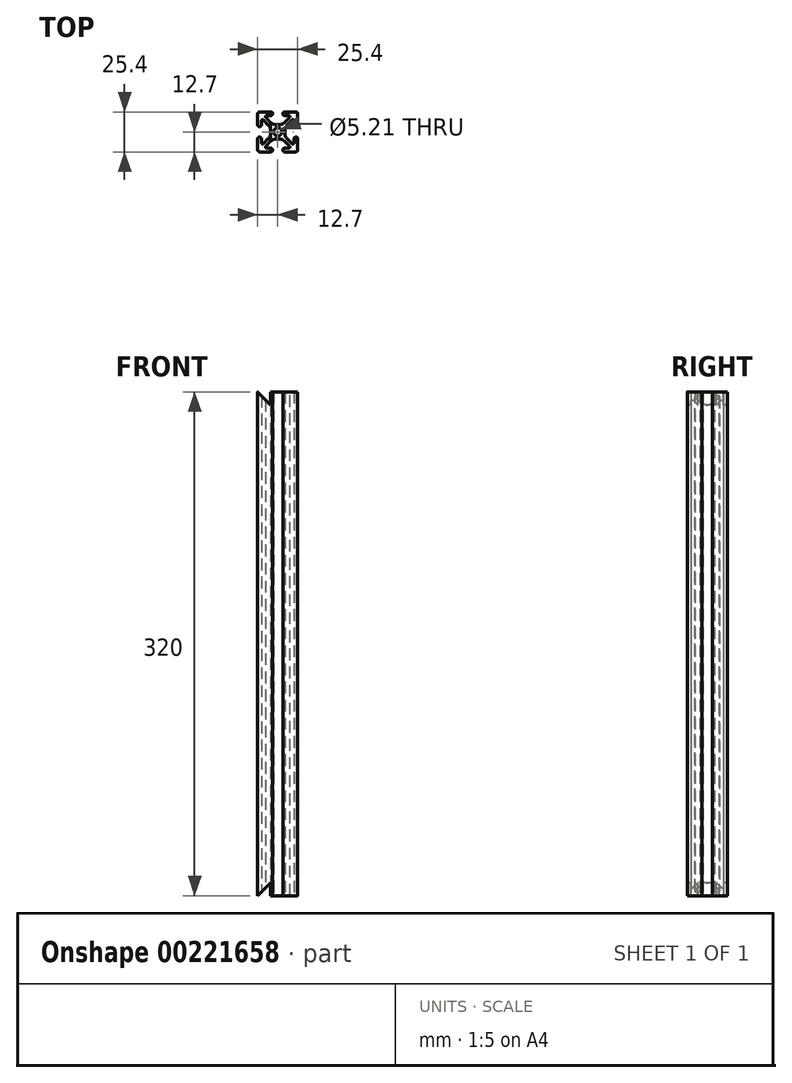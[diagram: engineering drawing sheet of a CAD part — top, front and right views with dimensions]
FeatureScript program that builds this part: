
annotation { "Feature Type Name" : "Feature", "Feature Type Description" : "" }
export const myFeature = defineFeature(function(context is Context, id is Id, definition is map)
    precondition{}
    {
        {
            var Q0;
            Q0=qCreatedBy(makeId("Top.planeOp"),FACE);
            var sketch = newSketch(context, id + "F0", { "sketchPlane" : qUnion([Q0])});
            skLineSegment(sketch, "E0.bottom", {"start": v(12.7, 12.7) * mm, "end": v(-12.7, 12.7) * mm});
            skLineSegment(sketch, "E0.top", {"start": v(12.7, -12.7) * mm, "end": v(-12.7, -12.7) * mm});
            skLineSegment(sketch, "E0.left", {"start": v(12.7, 12.7) * mm, "end": v(12.7, -12.7) * mm});
            skLineSegment(sketch, "E0.right", {"start": v(-12.7, 12.7) * mm, "end": v(-12.7, -12.7) * mm});
            skPoint(sketch, "E0.middle", {"position": v(0, 0) * mm});
            skCircle(sketch, "E1", {"center": v(0, 0) * mm, "radius": 2.6 * mm});
            skLineSegment(sketch, "E2", {"start": v(-12.7, 12.7) * mm, "end": v(12.7, -12.7) * mm, "construction": true});
            skLineSegment(sketch, "E3", {"start": v(0, 12.7) * mm, "end": v(0, -12.7) * mm, "construction": true});
            skLineSegment(sketch, "E4", {"start": v(-12.7, -12.7) * mm, "end": v(12.7, 12.7) * mm, "construction": true});
            skLineSegment(sketch, "E5", {"start": v(-8.78, 10.34) * mm, "end": v(-2.95, 4.5) * mm});
            skLineSegment(sketch, "E6.MirrorCS", {"start": v(8.78, 10.34) * mm, "end": v(2.95, 4.5) * mm});
            skLineSegment(sketch, "E7", {"start": v(-2.95, 4.5) * mm, "end": v(2.95, 4.5) * mm});
            skLineSegment(sketch, "E8.bottom", {"start": v(-3.24, 14.9) * mm, "end": v(3.24, 14.9) * mm});
            skLineSegment(sketch, "E8.left", {"start": v(-3.24, 14.9) * mm, "end": v(-3.24, 10.34) * mm});
            skLineSegment(sketch, "E8.right", {"start": v(3.24, 14.9) * mm, "end": v(3.24, 10.34) * mm});
            skLineSegment(sketch, "E9", {"start": v(-8.78, 10.34) * mm, "end": v(-3.24, 10.34) * mm});
            skLineSegment(sketch, "E10", {"start": v(3.24, 10.34) * mm, "end": v(8.78, 10.34) * mm});
            skLineSegment(sketch, "E11.MirrorCS", {"start": v(-10.34, 8.78) * mm, "end": v(-4.5, 2.95) * mm});
            skLineSegment(sketch, "E12.MirrorCS", {"start": v(-10.34, 8.78) * mm, "end": v(-10.34, 3.24) * mm});
            skLineSegment(sketch, "E13.MirrorCS", {"start": v(-14.9, 3.24) * mm, "end": v(-10.34, 3.24) * mm});
            skLineSegment(sketch, "E14.MirrorCS", {"start": v(-14.9, 3.24) * mm, "end": v(-14.9, -3.24) * mm});
            skLineSegment(sketch, "E15.MirrorCS", {"start": v(-14.9, -3.24) * mm, "end": v(-10.34, -3.24) * mm});
            skLineSegment(sketch, "E16.MirrorCS", {"start": v(-10.34, -3.24) * mm, "end": v(-10.34, -8.78) * mm});
            skLineSegment(sketch, "E17.MirrorCS", {"start": v(-10.34, -8.78) * mm, "end": v(-4.5, -2.95) * mm});
            skLineSegment(sketch, "E18.MirrorCS", {"start": v(-4.5, 2.95) * mm, "end": v(-4.5, -2.95) * mm});
            skLineSegment(sketch, "E19.MirrorCS", {"start": v(10.34, 8.78) * mm, "end": v(4.5, 2.95) * mm});
            skLineSegment(sketch, "E20.MirrorCS", {"start": v(4.5, -2.95) * mm, "end": v(4.5, 2.95) * mm});
            skLineSegment(sketch, "E21.MirrorCS", {"start": v(10.34, -8.78) * mm, "end": v(4.5, -2.95) * mm});
            skLineSegment(sketch, "E22.MirrorCS", {"start": v(10.34, -8.78) * mm, "end": v(10.34, -3.24) * mm});
            skLineSegment(sketch, "E23.MirrorCS", {"start": v(14.9, -3.24) * mm, "end": v(10.34, -3.24) * mm});
            skLineSegment(sketch, "E24.MirrorCS", {"start": v(14.9, -3.24) * mm, "end": v(14.9, 3.24) * mm});
            skLineSegment(sketch, "E25.MirrorCS", {"start": v(14.9, 3.24) * mm, "end": v(10.34, 3.24) * mm});
            skLineSegment(sketch, "E26.MirrorCS", {"start": v(10.34, 3.24) * mm, "end": v(10.34, 8.78) * mm});
            skLineSegment(sketch, "E27", {"start": v(-12.7, 0) * mm, "end": v(12.7, 0) * mm, "construction": true});
            skLineSegment(sketch, "E28.MirrorCS", {"start": v(-8.78, -10.34) * mm, "end": v(-2.95, -4.5) * mm});
            skLineSegment(sketch, "E29.MirrorCS", {"start": v(-8.78, -10.34) * mm, "end": v(-3.24, -10.34) * mm});
            skLineSegment(sketch, "E30.MirrorCS", {"start": v(-3.24, -14.9) * mm, "end": v(-3.24, -10.34) * mm});
            skLineSegment(sketch, "E31.MirrorCS", {"start": v(-3.24, -14.9) * mm, "end": v(3.24, -14.9) * mm});
            skLineSegment(sketch, "E32.MirrorCS", {"start": v(3.24, -14.9) * mm, "end": v(3.24, -10.34) * mm});
            skLineSegment(sketch, "E33.MirrorCS", {"start": v(3.24, -10.34) * mm, "end": v(8.78, -10.34) * mm});
            skLineSegment(sketch, "E34.MirrorCS", {"start": v(8.78, -10.34) * mm, "end": v(2.95, -4.5) * mm});
            skLineSegment(sketch, "E35.MirrorCS", {"start": v(-2.95, -4.5) * mm, "end": v(2.95, -4.5) * mm});
            skSolve(sketch);
        }
        {
            var Q0;
            Q0=makeQuery(id+"F0.imprint","IMPRINT",FACE,{"disambiguationData":[TD([[makeQuery(id+"F0.imprint","IMPRINT",EDGE,{"derivedFrom":sQuery(id+"F0.wireOp",EDGE,"E1")}),-1.0]])]});
            extrude(context, id + "F1", {"entities" : qUnion([Q0]), "depth" : 320 * mm});
        }
        {
            var Q0;
            Q0=makeQuery(id+"F1.opExtrude","SWEPT_EDGE",EDGE,{"disambiguationData":[OSD([sQuery(id+"F0.wireOp",EDGE,"E0.bottom"),sQuery(id+"F0.wireOp",EDGE,"E8.right")])]});
            var Q1;
            Q1=makeQuery(id+"F1.opExtrude","SWEPT_EDGE",EDGE,{"disambiguationData":[OSD([sQuery(id+"F0.wireOp",EDGE,"E8.right"),sQuery(id+"F0.wireOp",EDGE,"E10")])]});
            var Q2;
            Q2=makeQuery(id+"F1.opExtrude","SWEPT_EDGE",EDGE,{"disambiguationData":[OSD([sQuery(id+"F0.wireOp",EDGE,"E0.bottom"),sQuery(id+"F0.wireOp",EDGE,"E8.left")])]});
            var Q3;
            Q3=makeQuery(id+"F1.opExtrude","SWEPT_EDGE",EDGE,{"disambiguationData":[OSD([sQuery(id+"F0.wireOp",EDGE,"E0.right"),sQuery(id+"F0.wireOp",EDGE,"E13.MirrorCS")])]});
            var Q4;
            Q4=makeQuery(id+"F1.opExtrude","SWEPT_EDGE",EDGE,{"disambiguationData":[OSD([sQuery(id+"F0.wireOp",EDGE,"E8.left"),sQuery(id+"F0.wireOp",EDGE,"E9")])]});
            var Q5;
            Q5=makeQuery(id+"F1.opExtrude","SWEPT_EDGE",EDGE,{"disambiguationData":[OSD([sQuery(id+"F0.wireOp",EDGE,"E12.MirrorCS"),sQuery(id+"F0.wireOp",EDGE,"E13.MirrorCS")])]});
            var Q6;
            Q6=makeQuery(id+"F1.opExtrude","SWEPT_EDGE",EDGE,{"disambiguationData":[OSD([sQuery(id+"F0.wireOp",EDGE,"E0.left"),sQuery(id+"F0.wireOp",EDGE,"E25.MirrorCS")])]});
            var Q7;
            Q7=makeQuery(id+"F1.opExtrude","SWEPT_EDGE",EDGE,{"disambiguationData":[OSD([sQuery(id+"F0.wireOp",EDGE,"E25.MirrorCS"),sQuery(id+"F0.wireOp",EDGE,"E26.MirrorCS")])]});
            var Q8;
            Q8=makeQuery(id+"F1.opExtrude","SWEPT_EDGE",EDGE,{"disambiguationData":[OSD([sQuery(id+"F0.wireOp",EDGE,"E0.left"),sQuery(id+"F0.wireOp",EDGE,"E23.MirrorCS")])]});
            var Q9;
            Q9=makeQuery(id+"F1.opExtrude","SWEPT_EDGE",EDGE,{"disambiguationData":[OSD([sQuery(id+"F0.wireOp",EDGE,"E22.MirrorCS"),sQuery(id+"F0.wireOp",EDGE,"E23.MirrorCS")])]});
            var Q10;
            Q10=makeQuery(id+"F1.opExtrude","SWEPT_EDGE",EDGE,{"disambiguationData":[OSD([sQuery(id+"F0.wireOp",EDGE,"E32.MirrorCS"),sQuery(id+"F0.wireOp",EDGE,"E33.MirrorCS")])]});
            var Q11;
            Q11=makeQuery(id+"F1.opExtrude","SWEPT_EDGE",EDGE,{"disambiguationData":[OSD([sQuery(id+"F0.wireOp",EDGE,"E29.MirrorCS"),sQuery(id+"F0.wireOp",EDGE,"E30.MirrorCS")])]});
            var Q12;
            Q12=makeQuery(id+"F1.opExtrude","SWEPT_EDGE",EDGE,{"disambiguationData":[OSD([sQuery(id+"F0.wireOp",EDGE,"E15.MirrorCS"),sQuery(id+"F0.wireOp",EDGE,"E16.MirrorCS")])]});
            var Q13;
            Q13=makeQuery(id+"F1.opExtrude","SWEPT_EDGE",EDGE,{"disambiguationData":[OSD([sQuery(id+"F0.wireOp",EDGE,"E0.right"),sQuery(id+"F0.wireOp",EDGE,"E15.MirrorCS")])]});
            var Q14;
            Q14=makeQuery(id+"F1.opExtrude","SWEPT_EDGE",EDGE,{"disambiguationData":[OSD([sQuery(id+"F0.wireOp",EDGE,"E0.top"),sQuery(id+"F0.wireOp",EDGE,"E30.MirrorCS")])]});
            var Q15;
            Q15=makeQuery(id+"F1.opExtrude","SWEPT_EDGE",EDGE,{"disambiguationData":[OSD([sQuery(id+"F0.wireOp",EDGE,"E0.top"),sQuery(id+"F0.wireOp",EDGE,"E32.MirrorCS")])]});
            fillet(context, id + "F2", {"entities" : qUnion([Q0, Q1, Q2, Q3, Q4, Q5, Q6, Q7, Q8, Q9, Q10, Q11, Q12, Q13, Q14, Q15]), "radius" : 1.18 * mm, "tangentPropagation" : true, "allowEdgeOverflow" : false});
        }
        {
            var Q0;
            Q0=makeQuery(id+"F1.opExtrude","SWEPT_EDGE",EDGE,{"disambiguationData":[OSD([sQuery(id+"F0.wireOp",EDGE,"E6.MirrorCS"),sQuery(id+"F0.wireOp",EDGE,"E7")])]});
            var Q1;
            Q1=makeQuery(id+"F1.opExtrude","SWEPT_EDGE",EDGE,{"disambiguationData":[OSD([sQuery(id+"F0.wireOp",EDGE,"E5"),sQuery(id+"F0.wireOp",EDGE,"E7")])]});
            var Q2;
            Q2=makeQuery(id+"F1.opExtrude","SWEPT_EDGE",EDGE,{"disambiguationData":[OSD([sQuery(id+"F0.wireOp",EDGE,"E20.MirrorCS"),sQuery(id+"F0.wireOp",EDGE,"E21.MirrorCS")])]});
            var Q3;
            Q3=makeQuery(id+"F1.opExtrude","SWEPT_EDGE",EDGE,{"disambiguationData":[OSD([sQuery(id+"F0.wireOp",EDGE,"E19.MirrorCS"),sQuery(id+"F0.wireOp",EDGE,"E20.MirrorCS")])]});
            var Q4;
            Q4=makeQuery(id+"F1.opExtrude","SWEPT_EDGE",EDGE,{"disambiguationData":[OSD([sQuery(id+"F0.wireOp",EDGE,"E34.MirrorCS"),sQuery(id+"F0.wireOp",EDGE,"E35.MirrorCS")])]});
            var Q5;
            Q5=makeQuery(id+"F1.opExtrude","SWEPT_EDGE",EDGE,{"disambiguationData":[OSD([sQuery(id+"F0.wireOp",EDGE,"E28.MirrorCS"),sQuery(id+"F0.wireOp",EDGE,"E35.MirrorCS")])]});
            var Q6;
            Q6=makeQuery(id+"F1.opExtrude","SWEPT_EDGE",EDGE,{"disambiguationData":[OSD([sQuery(id+"F0.wireOp",EDGE,"E17.MirrorCS"),sQuery(id+"F0.wireOp",EDGE,"E18.MirrorCS")])]});
            var Q7;
            Q7=makeQuery(id+"F1.opExtrude","SWEPT_EDGE",EDGE,{"disambiguationData":[OSD([sQuery(id+"F0.wireOp",EDGE,"E11.MirrorCS"),sQuery(id+"F0.wireOp",EDGE,"E18.MirrorCS")])]});
            fillet(context, id + "F3", {"entities" : qUnion([Q0, Q1, Q2, Q3, Q4, Q5, Q6, Q7]), "radius" : 5.08 * mm, "tangentPropagation" : true, "allowEdgeOverflow" : false});
        }
        {
            var Q0;
            Q0=makeQuery(id+"F1.opExtrude","SWEPT_EDGE",EDGE,{"disambiguationData":[OSD([sQuery(id+"F0.wireOp",EDGE,"E6.MirrorCS"),sQuery(id+"F0.wireOp",EDGE,"E10")])]});
            var Q1;
            Q1=makeQuery(id+"F1.opExtrude","SWEPT_EDGE",EDGE,{"disambiguationData":[OSD([sQuery(id+"F0.wireOp",EDGE,"E5"),sQuery(id+"F0.wireOp",EDGE,"E9")])]});
            var Q2;
            Q2=makeQuery(id+"F1.opExtrude","SWEPT_EDGE",EDGE,{"disambiguationData":[OSD([sQuery(id+"F0.wireOp",EDGE,"E11.MirrorCS"),sQuery(id+"F0.wireOp",EDGE,"E12.MirrorCS")])]});
            var Q3;
            Q3=makeQuery(id+"F1.opExtrude","SWEPT_EDGE",EDGE,{"disambiguationData":[OSD([sQuery(id+"F0.wireOp",EDGE,"E16.MirrorCS"),sQuery(id+"F0.wireOp",EDGE,"E17.MirrorCS")])]});
            var Q4;
            Q4=makeQuery(id+"F1.opExtrude","SWEPT_EDGE",EDGE,{"disambiguationData":[OSD([sQuery(id+"F0.wireOp",EDGE,"E28.MirrorCS"),sQuery(id+"F0.wireOp",EDGE,"E29.MirrorCS")])]});
            var Q5;
            Q5=makeQuery(id+"F1.opExtrude","SWEPT_EDGE",EDGE,{"disambiguationData":[OSD([sQuery(id+"F0.wireOp",EDGE,"E33.MirrorCS"),sQuery(id+"F0.wireOp",EDGE,"E34.MirrorCS")])]});
            var Q6;
            Q6=makeQuery(id+"F1.opExtrude","SWEPT_EDGE",EDGE,{"disambiguationData":[OSD([sQuery(id+"F0.wireOp",EDGE,"E21.MirrorCS"),sQuery(id+"F0.wireOp",EDGE,"E22.MirrorCS")])]});
            var Q7;
            Q7=makeQuery(id+"F1.opExtrude","SWEPT_EDGE",EDGE,{"disambiguationData":[OSD([sQuery(id+"F0.wireOp",EDGE,"E19.MirrorCS"),sQuery(id+"F0.wireOp",EDGE,"E26.MirrorCS")])]});
            fillet(context, id + "F4", {"entities" : qUnion([Q0, Q1, Q2, Q3, Q4, Q5, Q6, Q7]), "radius" : 0.76 * mm, "tangentPropagation" : true, "allowEdgeOverflow" : false});
        }
        {
            var Q0;
            Q0=makeQuery(id+"F1.opExtrude","SWEPT_EDGE",EDGE,{"disambiguationData":[OSD([sQuery(id+"F0.wireOp",EDGE,"E0.top"),sQuery(id+"F0.wireOp",EDGE,"E0.right")])]});
            var Q1;
            Q1=makeQuery(id+"F1.opExtrude","SWEPT_EDGE",EDGE,{"disambiguationData":[OSD([sQuery(id+"F0.wireOp",EDGE,"E0.top"),sQuery(id+"F0.wireOp",EDGE,"E0.left")])]});
            var Q2;
            Q2=makeQuery(id+"F1.opExtrude","SWEPT_EDGE",EDGE,{"disambiguationData":[OSD([sQuery(id+"F0.wireOp",EDGE,"E0.bottom"),sQuery(id+"F0.wireOp",EDGE,"E0.left")])]});
            var Q3;
            Q3=makeQuery(id+"F1.opExtrude","SWEPT_EDGE",EDGE,{"disambiguationData":[OSD([sQuery(id+"F0.wireOp",EDGE,"E0.bottom"),sQuery(id+"F0.wireOp",EDGE,"E0.right")])]});
            fillet(context, id + "F5", {"entities" : qUnion([Q0, Q1, Q2, Q3]), "radius" : 1.27 * mm, "tangentPropagation" : true, "allowEdgeOverflow" : false});
        }
        {
            var Q0;
            {var subQ0=sQuery(id+"F0.wireOp",EDGE,"E0.top");Q0=makeQuery(id+"F1.opExtrude","SWEPT_FACE",FACE,{"disambiguationData":[OSD([subQ0]),TDD([makeQuery(id+"F0.imprint","IMPRINT",EDGE,{"disambiguationData":[TD([[makeQuery(id+"F0.imprint","INTERSECT",VERTEX,{"derivedFrom":[subQ0,sQuery(id+"F0.wireOp",EDGE,"E0.right")]}),1.0]])],"derivedFrom":subQ0})])]});}
            var sketch = newSketch(context, id + "F6", { "sketchPlane" : qUnion([Q0])});
            skLineSegment(sketch, "E36.0", {"start": v(-12.7, 0) * mm, "end": v(-12.7, 320) * mm});
            skPoint(sketch, "E37", {"position": v(-12.7, 0) * mm});
            skLineSegment(sketch, "E38.0", {"start": v(-4.42, 0) * mm, "end": v(-11.43, 0) * mm});
            skLineSegment(sketch, "E39.0", {"start": v(12.7, 320) * mm, "end": v(12.7, 0) * mm});
            skLineSegment(sketch, "E40", {"start": v(-12.7, 0) * mm, "end": v(12.7, 25.4) * mm});
            skLineSegment(sketch, "E41", {"start": v(12.7, 25.4) * mm, "end": v(12.7, 0) * mm});
            skLineSegment(sketch, "E42", {"start": v(-12.7, 0) * mm, "end": v(12.7, 0) * mm});
            skLineSegment(sketch, "E43", {"start": v(-12.7, 160) * mm, "end": v(12.7, 160) * mm, "construction": true});
            skLineSegment(sketch, "E44.MirrorCS", {"start": v(-12.7, 320) * mm, "end": v(12.7, 294.6) * mm});
            skLineSegment(sketch, "E45.MirrorCS", {"start": v(12.7, 294.6) * mm, "end": v(12.7, 320) * mm});
            skLineSegment(sketch, "E46.MirrorCS", {"start": v(-12.7, 320) * mm, "end": v(12.7, 320) * mm});
            skSolve(sketch);
        }
        {
            var Q0;
            {var subQ0=sQuery(id+"F6.wireOp",EDGE,"E40");var subQ1=sQuery(id+"F0.wireOp",EDGE,"E0.right");var subQ2=sQuery(id+"F0.wireOp",EDGE,"E0.top");var subQ4=makeQuery(id+"F1.opExtrude","SWEPT_FACE",FACE,{"disambiguationData":[OSD([subQ2]),TDD([makeQuery(id+"F0.imprint","IMPRINT",EDGE,{"disambiguationData":[TD([[makeQuery(id+"F0.imprint","INTERSECT",VERTEX,{"derivedFrom":[subQ2,subQ1]}),1.0]])],"derivedFrom":subQ2})])]});var subQ5=makeQuery(id+"F5.opFillet","BLEND_EDGE",EDGE,{"blendedFrom":[makeQuery(id+"F1.opExtrude","SWEPT_EDGE",EDGE,{"disambiguationData":[OSD([subQ2,subQ1])]}),subQ4],"blendedInto":[subQ4]});var subQ6=makeQuery(id+"F6.imprint","INTERSECT",VERTEX,{"derivedFrom":[subQ5,subQ0]});Q0=makeQuery(id+"F6.imprint","IMPRINT",FACE,{"disambiguationData":[TD([[makeQuery(id+"F6.imprint","IMPRINT",EDGE,{"disambiguationData":[TD([[subQ6,-1.0]])],"derivedFrom":subQ0}),-1.0]])]});}
            var Q1;
            {var subQ0=sQuery(id+"F6.wireOp",EDGE,"E42");var subQ1=sQuery(id+"F6.wireOp",EDGE,"E40");var subQ2=makeQuery(id+"F6.imprint","INTERSECT",VERTEX,{"derivedFrom":[subQ1,subQ0]});Q1=makeQuery(id+"F6.imprint","IMPRINT",FACE,{"disambiguationData":[TD([[makeQuery(id+"F6.imprint","IMPRINT",EDGE,{"disambiguationData":[TD([[subQ2,-1.0]])],"derivedFrom":subQ1}),-1.0]])]});}
            var Q2;
            {var subQ0=sQuery(id+"F6.wireOp",EDGE,"E41");Q2=makeQuery(id+"F6.imprint","IMPRINT",FACE,{"disambiguationData":[TD([[makeQuery(id+"F6.imprint","IMPRINT",EDGE,{"derivedFrom":subQ0}),-1.0]])]});}
            var Q3;
            {var subQ0=sQuery(id+"F6.wireOp",EDGE,"E45.MirrorCS");Q3=makeQuery(id+"F6.imprint","IMPRINT",FACE,{"disambiguationData":[TD([[makeQuery(id+"F6.imprint","IMPRINT",EDGE,{"derivedFrom":subQ0}),1.0]])]});}
            var Q4;
            {var subQ0=sQuery(id+"F6.wireOp",EDGE,"E44.MirrorCS");var subQ1=sQuery(id+"F0.wireOp",EDGE,"E0.right");var subQ2=sQuery(id+"F0.wireOp",EDGE,"E0.top");var subQ4=makeQuery(id+"F1.opExtrude","SWEPT_FACE",FACE,{"disambiguationData":[OSD([subQ2]),TDD([makeQuery(id+"F0.imprint","IMPRINT",EDGE,{"disambiguationData":[TD([[makeQuery(id+"F0.imprint","INTERSECT",VERTEX,{"derivedFrom":[subQ2,subQ1]}),1.0]])],"derivedFrom":subQ2})])]});var subQ5=makeQuery(id+"F5.opFillet","BLEND_EDGE",EDGE,{"blendedFrom":[makeQuery(id+"F1.opExtrude","SWEPT_EDGE",EDGE,{"disambiguationData":[OSD([subQ2,subQ1])]}),subQ4],"blendedInto":[subQ4]});var subQ6=makeQuery(id+"F6.imprint","INTERSECT",VERTEX,{"derivedFrom":[subQ5,subQ0]});Q4=makeQuery(id+"F6.imprint","IMPRINT",FACE,{"disambiguationData":[TD([[makeQuery(id+"F6.imprint","IMPRINT",EDGE,{"disambiguationData":[TD([[subQ6,-1.0]])],"derivedFrom":subQ0}),1.0]])]});}
            var Q5;
            {var subQ0=sQuery(id+"F6.wireOp",EDGE,"E46.MirrorCS");var subQ1=sQuery(id+"F6.wireOp",EDGE,"E44.MirrorCS");var subQ2=makeQuery(id+"F6.imprint","INTERSECT",VERTEX,{"derivedFrom":[sQuery(id+"F6.wireOp",EDGE,"E36.0"),subQ1,subQ0]});Q5=makeQuery(id+"F6.imprint","IMPRINT",FACE,{"disambiguationData":[TD([[makeQuery(id+"F6.imprint","IMPRINT",EDGE,{"disambiguationData":[TD([[subQ2,-1.0]])],"derivedFrom":subQ1}),1.0]])]});}
            extrude(context, id + "F7", {"entities" : qUnion([Q0, Q1, Q2, Q3, Q4, Q5]), "operationType" : NewBodyOperationType.REMOVE, "endBound" : BoundingType.THROUGH_ALL, "oppositeDirection" : true, "depth" : 25.4 * mm});
        }
    });
